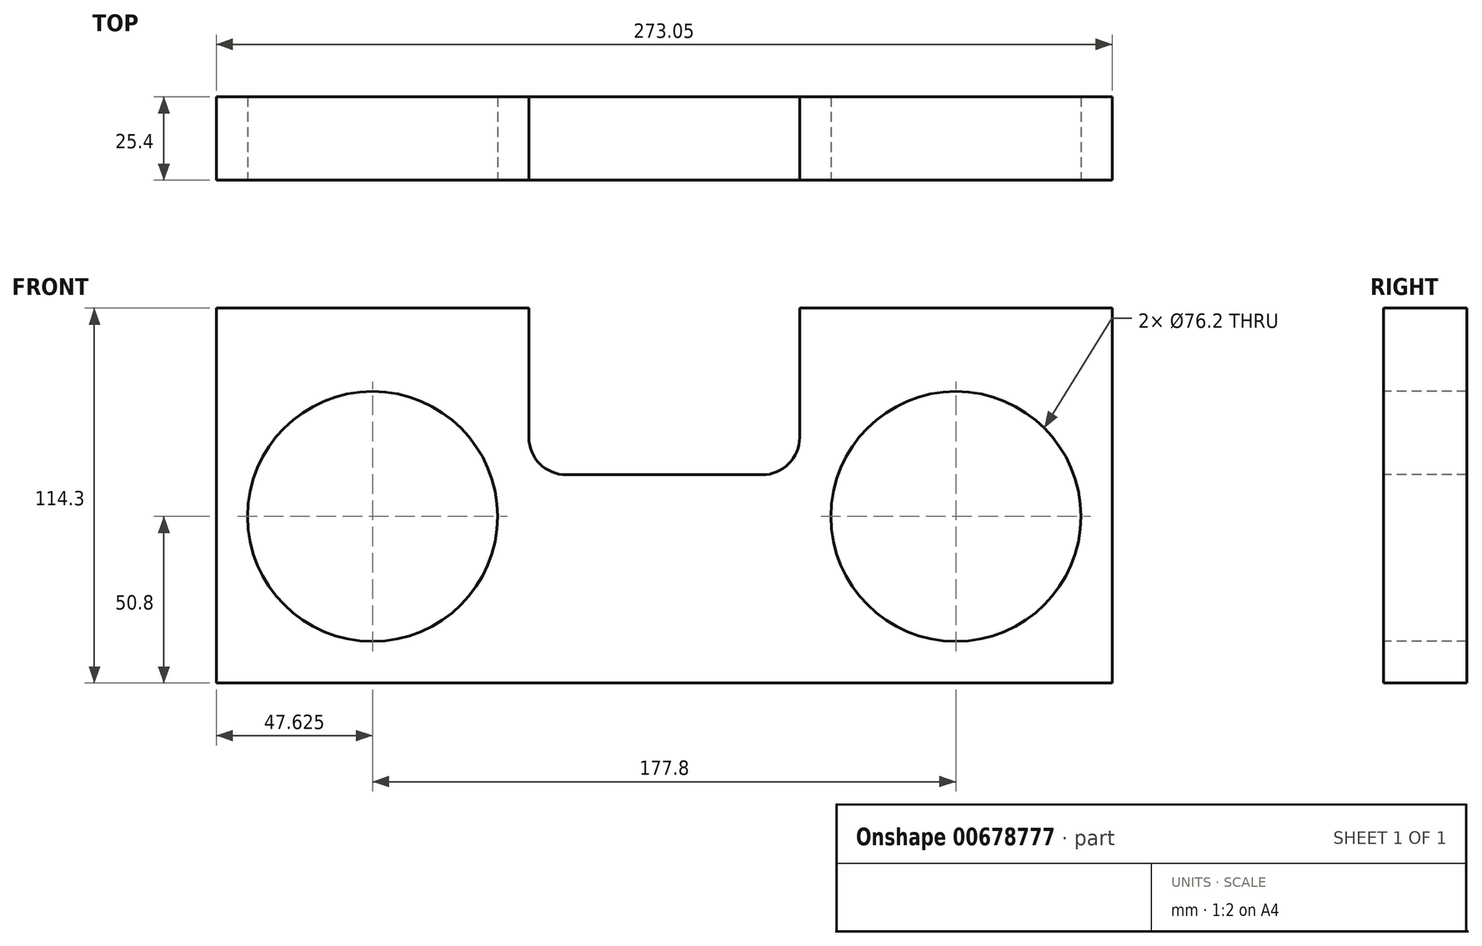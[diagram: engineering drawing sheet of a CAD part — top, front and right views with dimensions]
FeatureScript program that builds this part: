
annotation { "Feature Type Name" : "Feature", "Feature Type Description" : "" }
export const myFeature = defineFeature(function(context is Context, id is Id, definition is map)
    precondition{}
    {
        {
            var Q0;
            Q0=qCreatedBy(makeId("Front.planeOp"),FACE);
            var sketch = newSketch(context, id + "F0", { "sketchPlane" : qUnion([Q0])});
            skLineSegment(sketch, "E0.bottom", {"start": v(0, 0) * mm, "end": v(273.05, 0) * mm});
            skLineSegment(sketch, "E0.top", {"start": v(0, 114.3) * mm, "end": v(273.05, 114.3) * mm});
            skLineSegment(sketch, "E0.left", {"start": v(0, 0) * mm, "end": v(0, 114.3) * mm});
            skLineSegment(sketch, "E0.right", {"start": v(273.05, 0) * mm, "end": v(273.05, 114.3) * mm});
            skSolve(sketch);
        }
        {
            var Q0;
            Q0=makeQuery(id+"F0.imprint","IMPRINT",FACE,{"disambiguationData":[TD([[makeQuery(id+"F0.imprint","IMPRINT",EDGE,{"derivedFrom":sQuery(id+"F0.wireOp",EDGE,"E0.bottom")}),1.0]])]});
            extrude(context, id + "F1", {"entities" : qUnion([Q0]), "depth" : 25.4 * mm, "offsetDistance" : 25.4 * mm});
        }
        {
            var Q0;
            Q0=makeQuery(id+"F1.opExtrude","CAP_FACE",FACE,{"disambiguationData":[OSD([sQuery(id+"F0.wireOp",EDGE,"E0.bottom"),sQuery(id+"F0.wireOp",EDGE,"E0.top"),sQuery(id+"F0.wireOp",EDGE,"E0.left"),sQuery(id+"F0.wireOp",EDGE,"E0.right")])],"isStart":false});
            var sketch = newSketch(context, id + "F2", { "sketchPlane" : qUnion([Q0])});
            skCircle(sketch, "E1", {"center": v(47.62, 50.8) * mm, "radius": 38.1 * mm});
            skCircle(sketch, "E2", {"center": v(225.43, 50.8) * mm, "radius": 38.1 * mm});
            skSolve(sketch);
        }
        {
            var Q0;
            Q0=makeQuery(id+"F2.imprint","IMPRINT",FACE,{"disambiguationData":[TD([[makeQuery(id+"F2.imprint","IMPRINT",EDGE,{"derivedFrom":sQuery(id+"F2.wireOp",EDGE,"E1")}),1.0]])]});
            var Q1;
            Q1=makeQuery(id+"F2.imprint","IMPRINT",FACE,{"disambiguationData":[TD([[makeQuery(id+"F2.imprint","IMPRINT",EDGE,{"derivedFrom":sQuery(id+"F2.wireOp",EDGE,"E2")}),1.0]])]});
            extrude(context, id + "F3", {"entities" : qUnion([Q0, Q1]), "operationType" : NewBodyOperationType.REMOVE, "oppositeDirection" : true, "depth" : 25.4 * mm, "offsetDistance" : 25.4 * mm});
        }
        {
            var Q0;
            Q0=makeQuery(id+"F1.opExtrude","CAP_FACE",FACE,{"disambiguationData":[OSD([sQuery(id+"F0.wireOp",EDGE,"E0.bottom"),sQuery(id+"F0.wireOp",EDGE,"E0.top"),sQuery(id+"F0.wireOp",EDGE,"E0.left"),sQuery(id+"F0.wireOp",EDGE,"E0.right")])],"isStart":false});
            var sketch = newSketch(context, id + "F4", { "sketchPlane" : qUnion([Q0])});
            skLineSegment(sketch, "E3.bottom", {"start": v(95.25, 114.3) * mm, "end": v(177.8, 114.3) * mm});
            skLineSegment(sketch, "E3.top", {"start": v(106.68, 63.5) * mm, "end": v(166.37, 63.5) * mm});
            skLineSegment(sketch, "E3.left", {"start": v(95.25, 114.3) * mm, "end": v(95.25, 74.93) * mm});
            skLineSegment(sketch, "E3.right", {"start": v(177.8, 114.3) * mm, "end": v(177.8, 74.93) * mm});
            skPoint(sketch, "E4.visualSharp", {"position": v(95.25, 63.5) * mm});
            skArc(sketch, "E4.filletArc", {"start": v(95.25, 74.93) * mm, "mid": v(98.6, 66.85) * mm, "end": v(106.68, 63.5) * mm});
            skPoint(sketch, "E5.visualSharp", {"position": v(177.8, 63.5) * mm});
            skArc(sketch, "E5.filletArc", {"start": v(166.37, 63.5) * mm, "mid": v(174.45, 66.85) * mm, "end": v(177.8, 74.93) * mm});
            skLineSegment(sketch, "E6", {"start": v(177.8, 114.3) * mm, "end": v(273.05, 114.3) * mm});
            skLineSegment(sketch, "E7", {"start": v(273.05, 114.3) * mm, "end": v(177.8, 114.3) * mm});
            skSolve(sketch);
        }
        {
            var Q0;
            Q0=makeQuery(id+"F4.imprint","IMPRINT",FACE,{"disambiguationData":[TD([[makeQuery(id+"F4.imprint","IMPRINT",EDGE,{"derivedFrom":sQuery(id+"F4.wireOp",EDGE,"E3.bottom")}),-1.0]])]});
            extrude(context, id + "F5", {"entities" : qUnion([Q0]), "operationType" : NewBodyOperationType.REMOVE, "oppositeDirection" : true, "depth" : 25.4 * mm, "offsetDistance" : 25.4 * mm});
        }
    });
